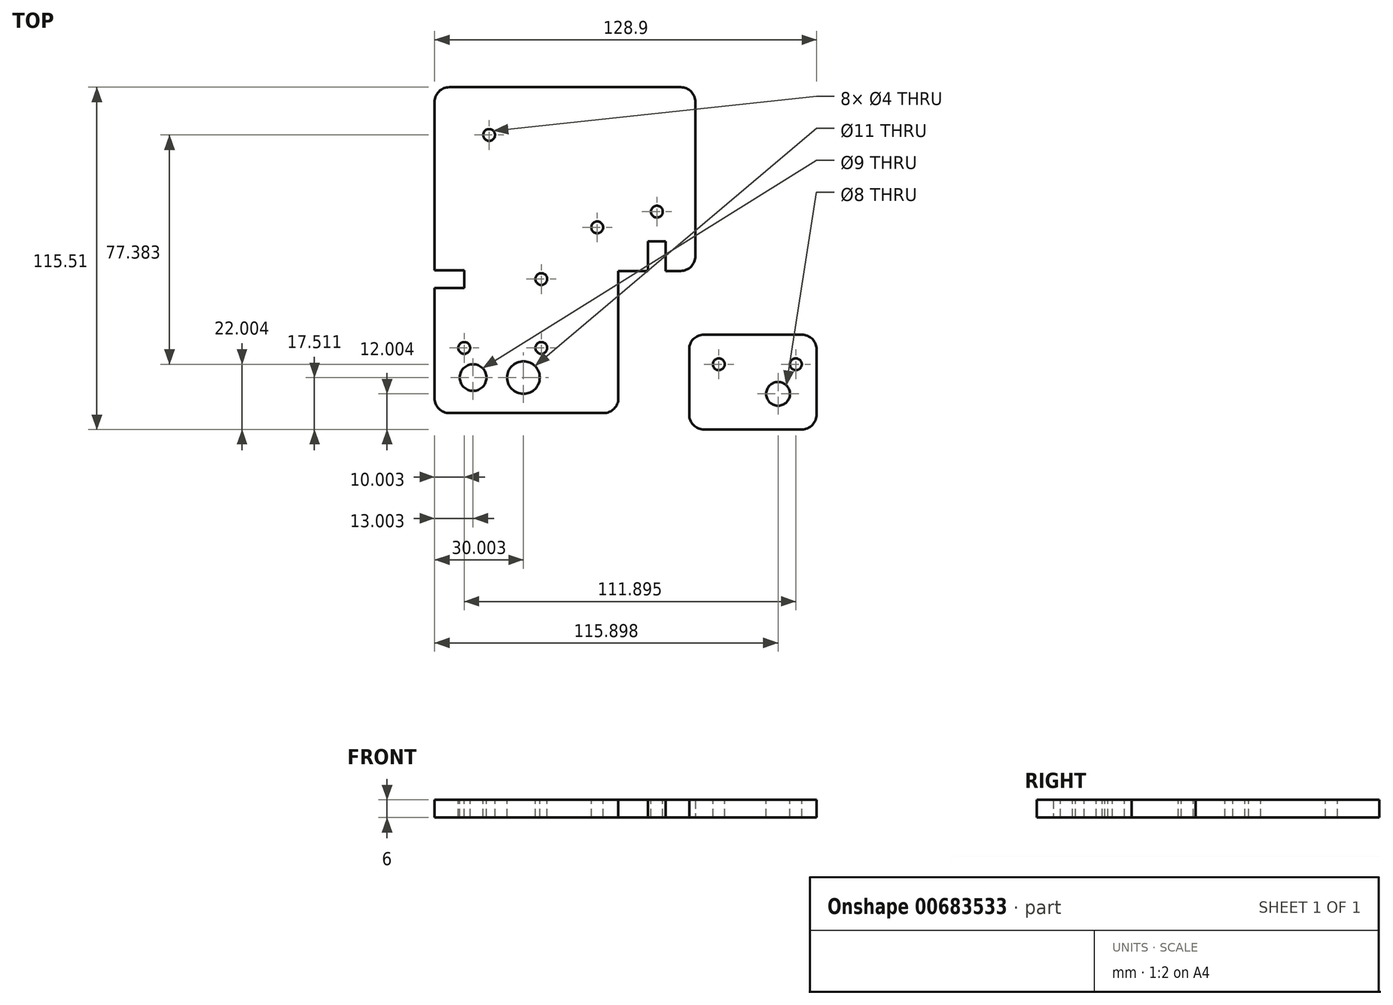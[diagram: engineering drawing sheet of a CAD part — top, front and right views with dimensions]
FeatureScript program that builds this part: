
annotation { "Feature Type Name" : "Feature", "Feature Type Description" : "" }
export const myFeature = defineFeature(function(context is Context, id is Id, definition is map)
    precondition{}
    {
        {
            var Q0;
            Q0=qCreatedBy(makeId("Top.planeOp"),FACE);
            var sketch = newSketch(context, id + "F0", { "sketchPlane" : qUnion([Q0])});
            skLineSegment(sketch, "E0.bottom", {"start": v(-3.4, -48.24) * mm, "end": v(-65.4, -48.24) * mm});
            skLineSegment(sketch, "E0.top", {"start": v(-3.4, 61.76) * mm, "end": v(-65.4, 61.76) * mm});
            skLineSegment(sketch, "E0.left", {"start": v(-3.4, -48.24) * mm, "end": v(-3.4, 61.76) * mm});
            skLineSegment(sketch, "E0.right", {"start": v(-65.4, -48.24) * mm, "end": v(-65.4, 61.76) * mm});
            skPoint(sketch, "E0.middle", {"position": v(-34.4, 6.76) * mm});
            skLineSegment(sketch, "E1.bottom", {"start": v(-3.4, 61.76) * mm, "end": v(22.6, 61.76) * mm});
            skLineSegment(sketch, "E1.top", {"start": v(-3.4, -0.24) * mm, "end": v(22.6, -0.24) * mm});
            skLineSegment(sketch, "E1.left", {"start": v(-3.4, 61.76) * mm, "end": v(-3.4, -0.24) * mm});
            skLineSegment(sketch, "E1.right", {"start": v(22.6, 61.76) * mm, "end": v(22.6, -0.24) * mm});
            skSolve(sketch);
        }
        {
            var Q0;
            Q0=makeQuery(id+"F0.imprint","IMPRINT",FACE,{"disambiguationData":[TD([[makeQuery(id+"F0.imprint","IMPRINT",EDGE,{"derivedFrom":sQuery(id+"F0.wireOp",EDGE,"E0.bottom")}),-1.0]])]});
            var Q1;
            Q1=makeQuery(id+"F0.imprint","IMPRINT",FACE,{"disambiguationData":[TD([[makeQuery(id+"F0.imprint","IMPRINT",EDGE,{"derivedFrom":sQuery(id+"F0.wireOp",EDGE,"E1.bottom")}),-1.0]])]});
            extrude(context, id + "F1", {"entities" : qUnion([Q0, Q1]), "depth" : 6 * mm, "offsetDistance" : 25 * mm});
        }
        {
            var Q0;
            Q0=makeQuery(id+"F1.opExtrude","CAP_FACE",FACE,{"disambiguationData":[OSD([sQuery(id+"F0.wireOp",EDGE,"E0.bottom"),sQuery(id+"F0.wireOp",EDGE,"E0.top"),sQuery(id+"F0.wireOp",EDGE,"E0.left"),sQuery(id+"F0.wireOp",EDGE,"E0.right"),sQuery(id+"F0.wireOp",EDGE,"E1.bottom"),sQuery(id+"F0.wireOp",EDGE,"E1.top"),sQuery(id+"F0.wireOp",EDGE,"E1.right")])],"isStart":false});
            var sketch = newSketch(context, id + "F2", { "sketchPlane" : qUnion([Q0])});
            skLineSegment(sketch, "E2.bottom", {"start": v(6.6, 9.76) * mm, "end": v(12.6, 9.76) * mm});
            skLineSegment(sketch, "E2.top", {"start": v(6.6, -10.24) * mm, "end": v(12.6, -10.24) * mm});
            skLineSegment(sketch, "E2.left", {"start": v(6.6, 9.76) * mm, "end": v(6.6, -10.24) * mm});
            skLineSegment(sketch, "E2.right", {"start": v(12.6, 9.76) * mm, "end": v(12.6, -10.24) * mm});
            skPoint(sketch, "E2.middle", {"position": v(9.6, -0.24) * mm});
            skLineSegment(sketch, "E3.bottom", {"start": v(-65.4, 0) * mm, "end": v(-55.4, 0) * mm});
            skLineSegment(sketch, "E3.top", {"start": v(-65.4, -6) * mm, "end": v(-55.4, -6) * mm});
            skLineSegment(sketch, "E3.left", {"start": v(-65.4, 0) * mm, "end": v(-65.4, -6) * mm});
            skLineSegment(sketch, "E3.right", {"start": v(-55.4, 0) * mm, "end": v(-55.4, -6) * mm});
            skSolve(sketch);
        }
        {
            var Q0;
            Q0=makeQuery(id+"F2.imprint","IMPRINT",FACE,{"disambiguationData":[TD([[makeQuery(id+"F2.imprint","IMPRINT",EDGE,{"derivedFrom":sQuery(id+"F2.wireOp",EDGE,"E3.bottom")}),-1.0]])]});
            var Q1;
            {var subQ0=sQuery(id+"F2.wireOp",EDGE,"E2.bottom");Q1=makeQuery(id+"F2.imprint","IMPRINT",FACE,{"disambiguationData":[TD([[makeQuery(id+"F2.imprint","IMPRINT",EDGE,{"derivedFrom":subQ0}),-1.0]])]});}
            extrude(context, id + "F3", {"entities" : qUnion([Q0, Q1]), "operationType" : NewBodyOperationType.REMOVE, "oppositeDirection" : true, "depth" : 25 * mm, "offsetDistance" : 25 * mm});
        }
        {
            var Q0;
            Q0=makeQuery(id+"F1.opExtrude","CAP_FACE",FACE,{"disambiguationData":[OSD([sQuery(id+"F0.wireOp",EDGE,"E0.bottom"),sQuery(id+"F0.wireOp",EDGE,"E0.top"),sQuery(id+"F0.wireOp",EDGE,"E0.left"),sQuery(id+"F0.wireOp",EDGE,"E0.right"),sQuery(id+"F0.wireOp",EDGE,"E1.bottom"),sQuery(id+"F0.wireOp",EDGE,"E1.top"),sQuery(id+"F0.wireOp",EDGE,"E1.right")])],"isStart":false});
            var sketch = newSketch(context, id + "F4", { "sketchPlane" : qUnion([Q0])});
            skCircle(sketch, "E4", {"center": v(-29.4, -3) * mm, "radius": 2 * mm});
            skPoint(sketch, "E4.centerSnap0", {"position": v(-55.4, -3) * mm});
            skCircle(sketch, "E5", {"center": v(9.6, 19.76) * mm, "radius": 2 * mm});
            skCircle(sketch, "E6", {"center": v(-52.4, -36.24) * mm, "radius": 4.5 * mm});
            skCircle(sketch, "E7", {"center": v(-35.4, -36.24) * mm, "radius": 5.5 * mm});
            skSolve(sketch);
        }
        {
            var Q0;
            Q0=makeQuery(id+"F4.imprint","IMPRINT",FACE,{"disambiguationData":[TD([[makeQuery(id+"F4.imprint","IMPRINT",EDGE,{"derivedFrom":sQuery(id+"F4.wireOp",EDGE,"E6")}),1.0]])]});
            var Q1;
            Q1=makeQuery(id+"F4.imprint","IMPRINT",FACE,{"disambiguationData":[TD([[makeQuery(id+"F4.imprint","IMPRINT",EDGE,{"derivedFrom":sQuery(id+"F4.wireOp",EDGE,"E7")}),1.0]])]});
            var Q2;
            Q2=makeQuery(id+"F4.imprint","IMPRINT",FACE,{"disambiguationData":[TD([[makeQuery(id+"F4.imprint","IMPRINT",EDGE,{"derivedFrom":sQuery(id+"F4.wireOp",EDGE,"E4")}),1.0]])]});
            var Q3;
            Q3=makeQuery(id+"F4.imprint","IMPRINT",FACE,{"disambiguationData":[TD([[makeQuery(id+"F4.imprint","IMPRINT",EDGE,{"derivedFrom":sQuery(id+"F4.wireOp",EDGE,"E5")}),1.0]])]});
            extrude(context, id + "F5", {"entities" : qUnion([Q0, Q1, Q2, Q3]), "operationType" : NewBodyOperationType.REMOVE, "oppositeDirection" : true, "depth" : 25 * mm, "offsetDistance" : 25 * mm});
        }
        {
            var Q0;
            Q0=makeQuery(id+"F1.opExtrude","SWEPT_EDGE",EDGE,{"disambiguationData":[OSD([sQuery(id+"F0.wireOp",EDGE,"E0.bottom"),sQuery(id+"F0.wireOp",EDGE,"E0.right")])]});
            var Q1;
            Q1=makeQuery(id+"F1.opExtrude","SWEPT_EDGE",EDGE,{"disambiguationData":[OSD([sQuery(id+"F0.wireOp",EDGE,"E0.bottom"),sQuery(id+"F0.wireOp",EDGE,"E0.left")])]});
            var Q2;
            Q2=makeQuery(id+"F1.opExtrude","SWEPT_EDGE",EDGE,{"disambiguationData":[OSD([sQuery(id+"F0.wireOp",EDGE,"E1.top"),sQuery(id+"F0.wireOp",EDGE,"E1.right")])]});
            var Q3;
            Q3=makeQuery(id+"F1.opExtrude","SWEPT_EDGE",EDGE,{"disambiguationData":[OSD([sQuery(id+"F0.wireOp",EDGE,"E1.bottom"),sQuery(id+"F0.wireOp",EDGE,"E1.right")])]});
            var Q4;
            Q4=makeQuery(id+"F1.opExtrude","SWEPT_EDGE",EDGE,{"disambiguationData":[OSD([sQuery(id+"F0.wireOp",EDGE,"E0.top"),sQuery(id+"F0.wireOp",EDGE,"E0.right")])]});
            fillet(context, id + "F6", {"entities" : qUnion([Q0, Q1, Q2, Q3, Q4]), "radius" : 5 * mm, "tangentPropagation" : true, "allowEdgeOverflow" : false});
        }
        {
            var Q0;
            Q0=makeQuery(id+"F1.opExtrude","CAP_FACE",FACE,{"disambiguationData":[OSD([sQuery(id+"F0.wireOp",EDGE,"E0.bottom"),sQuery(id+"F0.wireOp",EDGE,"E0.top"),sQuery(id+"F0.wireOp",EDGE,"E0.left"),sQuery(id+"F0.wireOp",EDGE,"E0.right"),sQuery(id+"F0.wireOp",EDGE,"E1.bottom"),sQuery(id+"F0.wireOp",EDGE,"E1.top"),sQuery(id+"F0.wireOp",EDGE,"E1.right")])],"isStart":false});
            var sketch = newSketch(context, id + "F7", { "sketchPlane" : qUnion([Q0])});
            skCircle(sketch, "E8", {"center": v(-55.4, -26.24) * mm, "radius": 2 * mm});
            skCircle(sketch, "E9", {"center": v(-29.4, -26.24) * mm, "radius": 2 * mm});
            skSolve(sketch);
        }
        {
            var Q0;
            Q0=makeQuery(id+"F7.imprint","IMPRINT",FACE,{"disambiguationData":[TD([[makeQuery(id+"F7.imprint","IMPRINT",EDGE,{"derivedFrom":sQuery(id+"F7.wireOp",EDGE,"E8")}),1.0]])]});
            var Q1;
            Q1=makeQuery(id+"F7.imprint","IMPRINT",FACE,{"disambiguationData":[TD([[makeQuery(id+"F7.imprint","IMPRINT",EDGE,{"derivedFrom":sQuery(id+"F7.wireOp",EDGE,"E9")}),1.0]])]});
            extrude(context, id + "F8", {"entities" : qUnion([Q0, Q1]), "operationType" : NewBodyOperationType.REMOVE, "oppositeDirection" : true, "depth" : 25 * mm, "offsetDistance" : 25 * mm});
        }
        {
            var Q0;
            Q0=qCreatedBy(makeId("Top.planeOp"),FACE);
            var sketch = newSketch(context, id + "F9", { "sketchPlane" : qUnion([Q0])});
            skLineSegment(sketch, "E10.bottom", {"start": v(20.49, -21.75) * mm, "end": v(63.49, -21.75) * mm});
            skLineSegment(sketch, "E10.top", {"start": v(20.49, -53.75) * mm, "end": v(63.49, -53.75) * mm});
            skLineSegment(sketch, "E10.left", {"start": v(20.49, -21.75) * mm, "end": v(20.49, -53.75) * mm});
            skLineSegment(sketch, "E10.right", {"start": v(63.49, -21.75) * mm, "end": v(63.49, -53.75) * mm});
            skSolve(sketch);
        }
        {
            var Q0;
            Q0=makeQuery(id+"F9.imprint","IMPRINT",FACE,{"disambiguationData":[TD([[makeQuery(id+"F9.imprint","IMPRINT",EDGE,{"derivedFrom":sQuery(id+"F9.wireOp",EDGE,"E10.bottom")}),-1.0]])]});
            extrude(context, id + "F10", {"entities" : qUnion([Q0]), "depth" : 6 * mm, "offsetDistance" : 25 * mm});
        }
        {
            var Q0;
            Q0=makeQuery(id+"F10.opExtrude","CAP_FACE",FACE,{"disambiguationData":[OSD([sQuery(id+"F9.wireOp",EDGE,"E10.bottom"),sQuery(id+"F9.wireOp",EDGE,"E10.top"),sQuery(id+"F9.wireOp",EDGE,"E10.left"),sQuery(id+"F9.wireOp",EDGE,"E10.right")])],"isStart":false});
            var sketch = newSketch(context, id + "F11", { "sketchPlane" : qUnion([Q0])});
            skCircle(sketch, "E11", {"center": v(50.49, -41.75) * mm, "radius": 4 * mm});
            skCircle(sketch, "E12", {"center": v(30.49, -31.75) * mm, "radius": 2 * mm});
            skCircle(sketch, "E13", {"center": v(56.49, -31.75) * mm, "radius": 2 * mm});
            skSolve(sketch);
        }
        {
            var Q0;
            Q0=makeQuery(id+"F11.imprint","IMPRINT",FACE,{"disambiguationData":[TD([[makeQuery(id+"F11.imprint","IMPRINT",EDGE,{"derivedFrom":sQuery(id+"F11.wireOp",EDGE,"E12")}),1.0]])]});
            var Q1;
            Q1=makeQuery(id+"F11.imprint","IMPRINT",FACE,{"disambiguationData":[TD([[makeQuery(id+"F11.imprint","IMPRINT",EDGE,{"derivedFrom":sQuery(id+"F11.wireOp",EDGE,"E11")}),1.0]])]});
            var Q2;
            Q2=makeQuery(id+"F11.imprint","IMPRINT",FACE,{"disambiguationData":[TD([[makeQuery(id+"F11.imprint","IMPRINT",EDGE,{"derivedFrom":sQuery(id+"F11.wireOp",EDGE,"E13")}),1.0]])]});
            extrude(context, id + "F12", {"entities" : qUnion([Q0, Q1, Q2]), "operationType" : NewBodyOperationType.REMOVE, "oppositeDirection" : true, "depth" : 25 * mm, "offsetDistance" : 25 * mm});
        }
        {
            var Q0;
            Q0=makeQuery(id+"F10.opExtrude","SWEPT_EDGE",EDGE,{"disambiguationData":[OSD([sQuery(id+"F9.wireOp",EDGE,"E10.top"),sQuery(id+"F9.wireOp",EDGE,"E10.left")])]});
            var Q1;
            Q1=makeQuery(id+"F10.opExtrude","SWEPT_EDGE",EDGE,{"disambiguationData":[OSD([sQuery(id+"F9.wireOp",EDGE,"E10.top"),sQuery(id+"F9.wireOp",EDGE,"E10.right")])]});
            var Q2;
            Q2=makeQuery(id+"F10.opExtrude","SWEPT_EDGE",EDGE,{"disambiguationData":[OSD([sQuery(id+"F9.wireOp",EDGE,"E10.bottom"),sQuery(id+"F9.wireOp",EDGE,"E10.right")])]});
            var Q3;
            Q3=makeQuery(id+"F10.opExtrude","SWEPT_EDGE",EDGE,{"disambiguationData":[OSD([sQuery(id+"F9.wireOp",EDGE,"E10.bottom"),sQuery(id+"F9.wireOp",EDGE,"E10.left")])]});
            fillet(context, id + "F13", {"entities" : qUnion([Q0, Q1, Q2, Q3]), "radius" : 5 * mm, "tangentPropagation" : true, "allowEdgeOverflow" : false});
        }
        {
            var Q0;
            Q0=makeQuery(id+"F7.imprint","IMPRINT",FACE,{"disambiguationData":[TD([[makeQuery(id+"F7.imprint","IMPRINT",EDGE,{"derivedFrom":sQuery(id+"F7.wireOp",EDGE,"E8")}),-1.0]])]});
            var sketch = newSketch(context, id + "F14", { "sketchPlane" : qUnion([Q0])});
            skLineSegment(sketch, "E14", {"start": v(4.43, 1.65) * mm, "end": v(-66.16, 62.02) * mm, "construction": true});
            skCircle(sketch, "E15", {"center": v(-47, 45.64) * mm, "radius": 2 * mm});
            skCircle(sketch, "E16", {"center": v(-10.53, 14.44) * mm, "radius": 2 * mm});
            skSolve(sketch);
        }
        {
            var Q0;
            Q0 = qSketchRegion(id + "F14", true);
            extrude(context, id + "F15", {"entities" : qUnion([Q0]), "operationType" : NewBodyOperationType.REMOVE, "oppositeDirection" : true, "depth" : 25 * mm, "offsetDistance" : 25 * mm});
        }
    });
